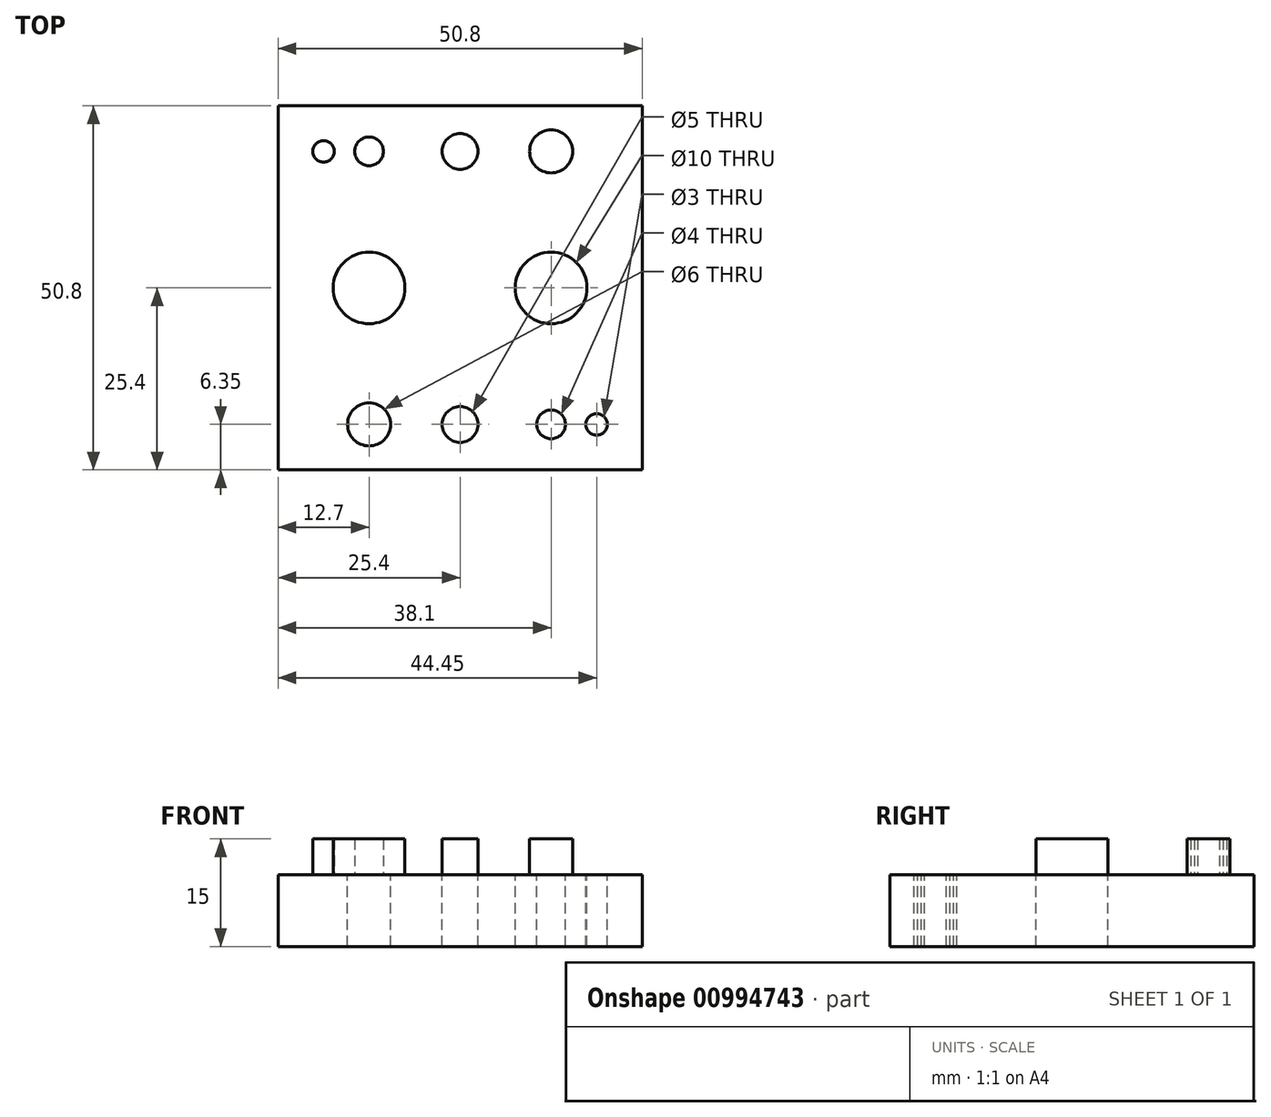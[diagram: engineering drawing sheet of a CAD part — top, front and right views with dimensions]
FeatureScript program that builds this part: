
annotation { "Feature Type Name" : "Feature", "Feature Type Description" : "" }
export const myFeature = defineFeature(function(context is Context, id is Id, definition is map)
    precondition{}
    {
        {
            var Q0;
            Q0=qCreatedBy(makeId("Top.planeOp"),FACE);
            var sketch = newSketch(context, id + "F0", { "sketchPlane" : qUnion([Q0])});
            skLineSegment(sketch, "E0.bottom", {"start": v(25.4, -25.4) * mm, "end": v(-25.4, -25.4) * mm});
            skLineSegment(sketch, "E0.top", {"start": v(25.4, 25.4) * mm, "end": v(-25.4, 25.4) * mm});
            skLineSegment(sketch, "E0.left", {"start": v(25.4, -25.4) * mm, "end": v(25.4, 25.4) * mm});
            skLineSegment(sketch, "E0.right", {"start": v(-25.4, -25.4) * mm, "end": v(-25.4, 25.4) * mm});
            skLineSegment(sketch, "E1.bottom", {"start": v(19.05, -19.05) * mm, "end": v(-19.05, -19.05) * mm, "construction": true});
            skLineSegment(sketch, "E1.top", {"start": v(19.05, 19.05) * mm, "end": v(-19.05, 19.05) * mm, "construction": true});
            skLineSegment(sketch, "E1.left", {"start": v(19.05, -19.05) * mm, "end": v(19.05, 19.05) * mm, "construction": true});
            skLineSegment(sketch, "E1.right", {"start": v(-19.05, -19.05) * mm, "end": v(-19.05, 19.05) * mm, "construction": true});
            skLineSegment(sketch, "E2.bottom", {"start": v(12.7, -12.7) * mm, "end": v(-12.7, -12.7) * mm, "construction": true});
            skLineSegment(sketch, "E2.top", {"start": v(12.7, 12.7) * mm, "end": v(-12.7, 12.7) * mm, "construction": true});
            skLineSegment(sketch, "E2.left", {"start": v(12.7, -12.7) * mm, "end": v(12.7, 12.7) * mm, "construction": true});
            skLineSegment(sketch, "E2.right", {"start": v(-12.7, -12.7) * mm, "end": v(-12.7, 12.7) * mm, "construction": true});
            skCircle(sketch, "E3", {"center": v(-19.05, 19.05) * mm, "radius": 1.5 * mm});
            skCircle(sketch, "E4", {"center": v(-12.7, 19.05) * mm, "radius": 2 * mm});
            skCircle(sketch, "E5", {"center": v(0, 19.05) * mm, "radius": 2.5 * mm});
            skCircle(sketch, "E6", {"center": v(12.7, 19.05) * mm, "radius": 3 * mm});
            skCircle(sketch, "E7", {"center": v(0, -19.05) * mm, "radius": 2.5 * mm});
            skPoint(sketch, "E8.middle", {"position": v(-19.05, 0) * mm});
            skCircle(sketch, "E9", {"center": v(12.7, 0) * mm, "radius": 5 * mm});
            skCircle(sketch, "E10", {"center": v(-12.7, 0) * mm, "radius": 5 * mm});
            skCircle(sketch, "E11.MirrorC", {"center": v(19.05, -19.05) * mm, "radius": 1.5 * mm});
            skCircle(sketch, "E12.MirrorC", {"center": v(12.7, -19.05) * mm, "radius": 2 * mm});
            skCircle(sketch, "E13.MirrorC", {"center": v(-12.7, -19.05) * mm, "radius": 3 * mm});
            skSolve(sketch);
        }
        {
            var Q0;
            Q0 = qSketchRegion(id + "F0", true);
            var Q1;
            Q1=makeQuery(id+"F0.imprint","IMPRINT",FACE,{"disambiguationData":[TD([[makeQuery(id+"F0.imprint","IMPRINT",EDGE,{"derivedFrom":sQuery(id+"F0.wireOp",EDGE,"E6")}),1.0]])]});
            var Q2;
            Q2=makeQuery(id+"F0.imprint","IMPRINT",FACE,{"disambiguationData":[TD([[makeQuery(id+"F0.imprint","IMPRINT",EDGE,{"derivedFrom":sQuery(id+"F0.wireOp",EDGE,"E5")}),1.0]])]});
            var Q3;
            Q3=makeQuery(id+"F0.imprint","IMPRINT",FACE,{"disambiguationData":[TD([[makeQuery(id+"F0.imprint","IMPRINT",EDGE,{"derivedFrom":sQuery(id+"F0.wireOp",EDGE,"E4")}),1.0]])]});
            var Q4;
            Q4=makeQuery(id+"F0.imprint","IMPRINT",FACE,{"disambiguationData":[TD([[makeQuery(id+"F0.imprint","IMPRINT",EDGE,{"derivedFrom":sQuery(id+"F0.wireOp",EDGE,"E3")}),1.0]])]});
            var Q5;
            Q5=makeQuery(id+"F0.imprint","IMPRINT",FACE,{"disambiguationData":[TD([[makeQuery(id+"F0.imprint","IMPRINT",EDGE,{"derivedFrom":sQuery(id+"F0.wireOp",EDGE,"E10")}),1.0]])]});
            extrude(context, id + "F1", {"entities" : qUnion([Q0, Q1, Q2, Q3, Q4, Q5]), "oppositeDirection" : true, "depth" : 10 * mm, "offsetDistance" : 25.4 * mm});
        }
        {
            var Q0;
            Q0=makeQuery(id+"F0.imprint","IMPRINT",FACE,{"disambiguationData":[TD([[makeQuery(id+"F0.imprint","IMPRINT",EDGE,{"derivedFrom":sQuery(id+"F0.wireOp",EDGE,"E10")}),1.0]])]});
            var Q1;
            Q1=makeQuery(id+"F0.imprint","IMPRINT",FACE,{"disambiguationData":[TD([[makeQuery(id+"F0.imprint","IMPRINT",EDGE,{"derivedFrom":sQuery(id+"F0.wireOp",EDGE,"E6")}),1.0]])]});
            var Q2;
            Q2=makeQuery(id+"F0.imprint","IMPRINT",FACE,{"disambiguationData":[TD([[makeQuery(id+"F0.imprint","IMPRINT",EDGE,{"derivedFrom":sQuery(id+"F0.wireOp",EDGE,"E5")}),1.0]])]});
            var Q3;
            Q3=makeQuery(id+"F0.imprint","IMPRINT",FACE,{"disambiguationData":[TD([[makeQuery(id+"F0.imprint","IMPRINT",EDGE,{"derivedFrom":sQuery(id+"F0.wireOp",EDGE,"E4")}),1.0]])]});
            var Q4;
            Q4=makeQuery(id+"F0.imprint","IMPRINT",FACE,{"disambiguationData":[TD([[makeQuery(id+"F0.imprint","IMPRINT",EDGE,{"derivedFrom":sQuery(id+"F0.wireOp",EDGE,"E3")}),1.0]])]});
            extrude(context, id + "F2", {"entities" : qUnion([Q0, Q1, Q2, Q3, Q4]), "depth" : 5 * mm, "offsetDistance" : 25.4 * mm});
        }
    });
